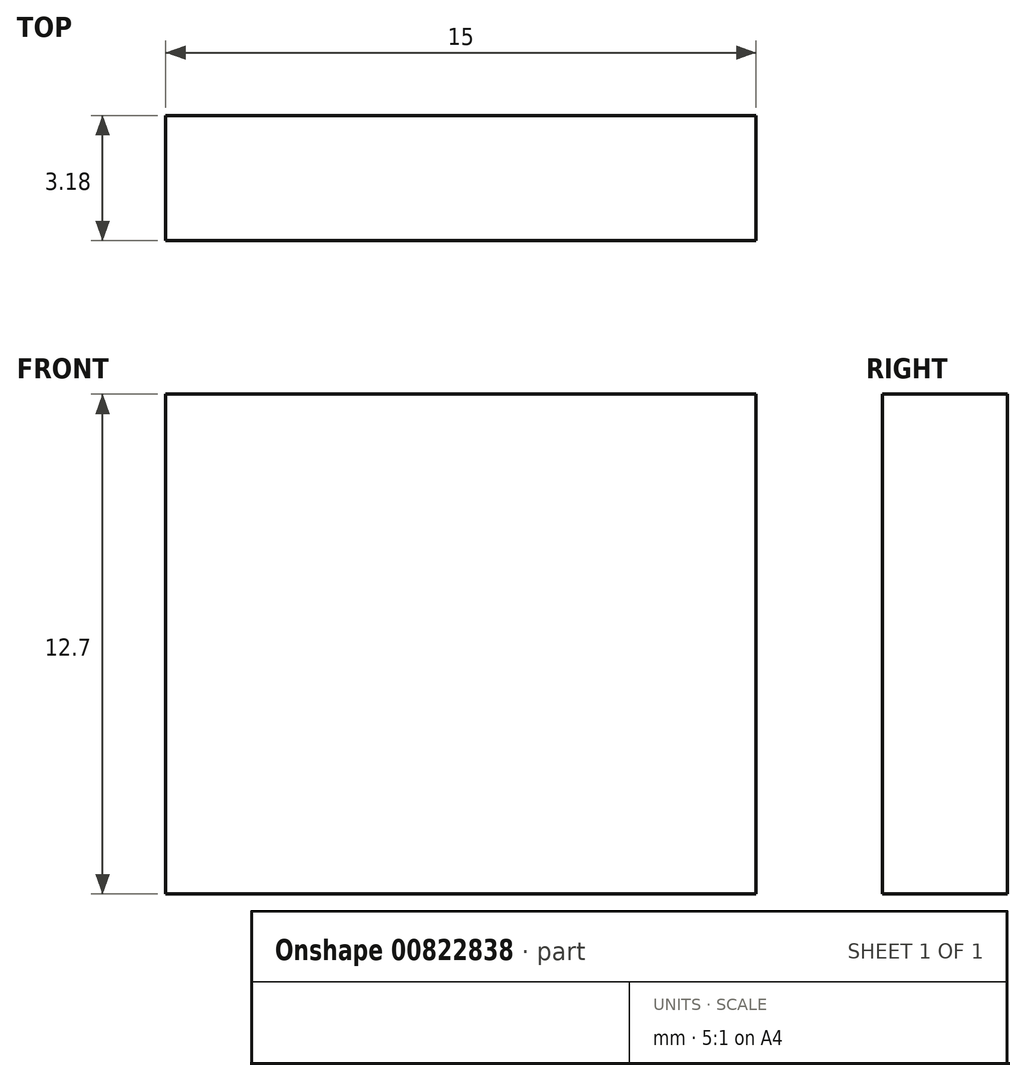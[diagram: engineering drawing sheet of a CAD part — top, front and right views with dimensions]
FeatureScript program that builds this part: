
annotation { "Feature Type Name" : "Feature", "Feature Type Description" : "" }
export const myFeature = defineFeature(function(context is Context, id is Id, definition is map)
    precondition{}
    {
        {
            var Q0;
            Q0=qCreatedBy(makeId("Front.planeOp"),FACE);
            var sketch = newSketch(context, id + "F0", { "sketchPlane" : qUnion([Q0])});
            skLineSegment(sketch, "E0.bottom", {"start": v(-7.5, -6.35) * mm, "end": v(7.5, -6.35) * mm});
            skLineSegment(sketch, "E0.top", {"start": v(-7.5, 6.35) * mm, "end": v(7.5, 6.35) * mm});
            skLineSegment(sketch, "E0.left", {"start": v(-7.5, -6.35) * mm, "end": v(-7.5, 6.35) * mm});
            skLineSegment(sketch, "E0.right", {"start": v(7.5, -6.35) * mm, "end": v(7.5, 6.35) * mm});
            skPoint(sketch, "E0.middle", {"position": v(0, 0) * mm});
            skSolve(sketch);
        }
        {
            var Q0;
            Q0 = qSketchRegion(id + "F0", true);
            extrude(context, id + "F1", {"entities" : qUnion([Q0]), "endBound" : BoundingType.SYMMETRIC, "depth" : (25.4 / 8) * mm, "offsetDistance" : 25 * mm});
        }
    });
